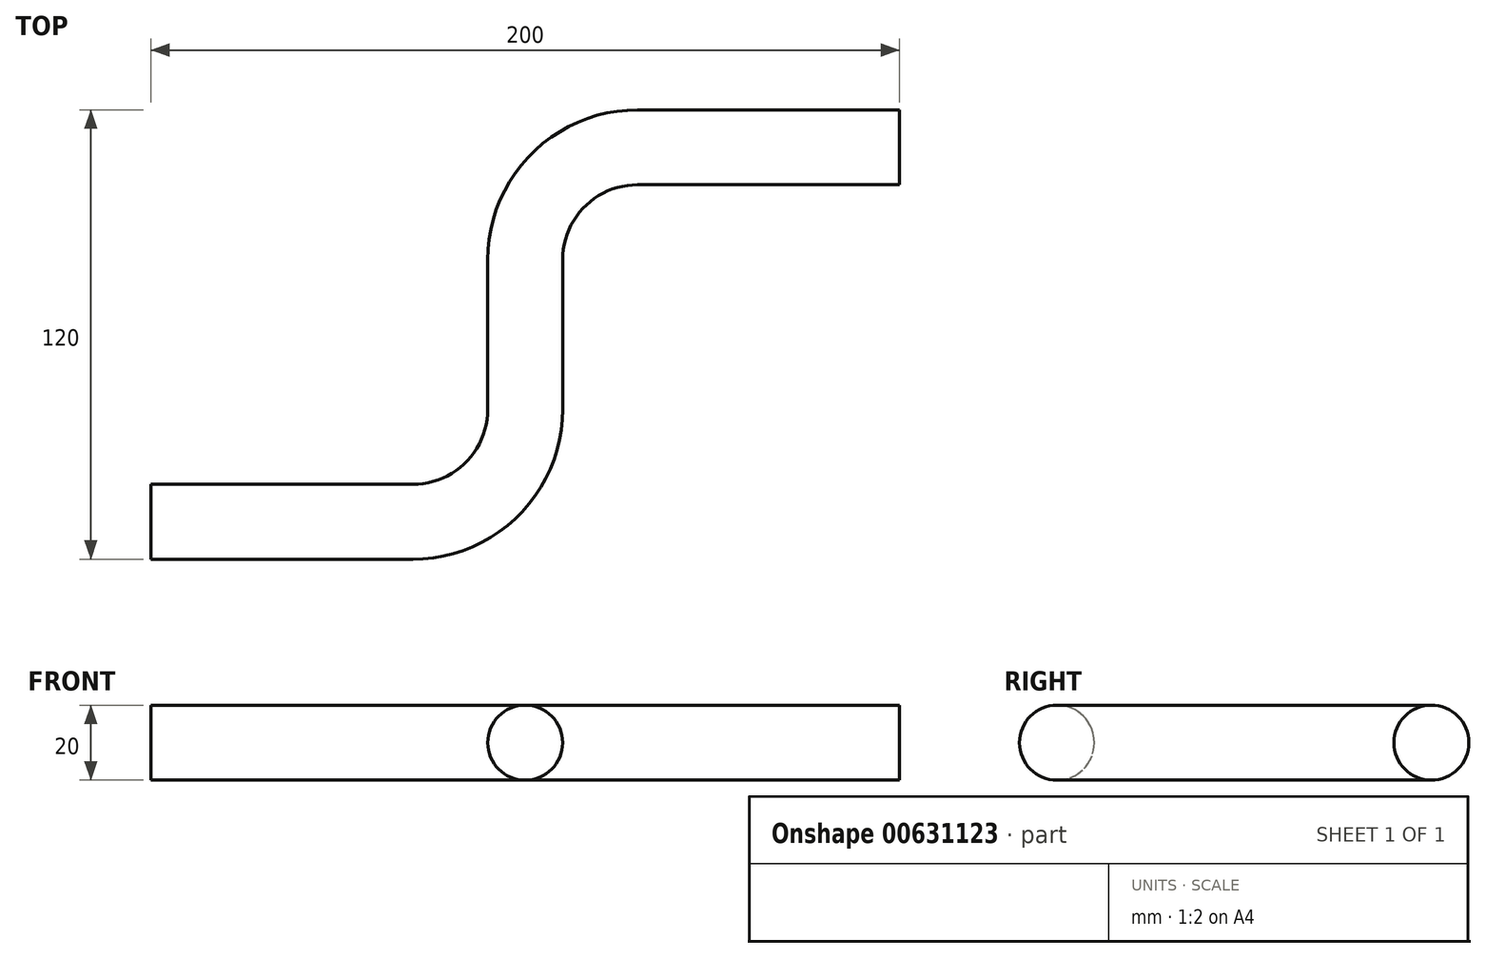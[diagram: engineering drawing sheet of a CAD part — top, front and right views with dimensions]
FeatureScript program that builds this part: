
annotation { "Feature Type Name" : "Feature", "Feature Type Description" : "" }
export const myFeature = defineFeature(function(context is Context, id is Id, definition is map)
    precondition{}
    {
        {
            var Q0;
            Q0=qCreatedBy(makeId("Top.planeOp"),FACE);
            var sketch = newSketch(context, id + "F0", { "sketchPlane" : qUnion([Q0])});
            skLineSegment(sketch, "E0", {"start": v(0, 0) * mm, "end": v(70, 0) * mm});
            skArc(sketch, "E1", {"start": v(70, 0) * mm, "mid": v(91.21, 8.79) * mm, "end": v(100, 30) * mm});
            skLineSegment(sketch, "E2", {"start": v(100, 30) * mm, "end": v(100, 70) * mm});
            skArc(sketch, "E3", {"start": v(130, 100) * mm, "mid": v(108.79, 91.21) * mm, "end": v(100, 70) * mm});
            skLineSegment(sketch, "E4", {"start": v(130, 100) * mm, "end": v(200, 100) * mm});
            skSolve(sketch);
        }
        {
            var Q0;
            Q0=qCreatedBy(makeId("Right.planeOp"),FACE);
            var sketch = newSketch(context, id + "F1", { "sketchPlane" : qUnion([Q0])});
            skCircle(sketch, "E5", {"center": v(0, 0) * mm, "radius": 10 * mm});
            skSolve(sketch);
        }
        {
            var Q0;
            Q0=makeQuery(id+"F1.imprint","IMPRINT",FACE,{"disambiguationData":[TD([[makeQuery(id+"F1.imprint","IMPRINT",EDGE,{"derivedFrom":sQuery(id+"F1.wireOp",EDGE,"E5")}),1.0]])]});
            var Q1;
            Q1 = qConstructionFilter(qBodyType(qCreatedBy(id + "F0" ,EDGE), BodyType.WIRE), ConstructionObject.NO);
            sweep(context, id + "F2", {"profiles" : qUnion([Q0]), "path" : qUnion([Q1])});
        }
    });
